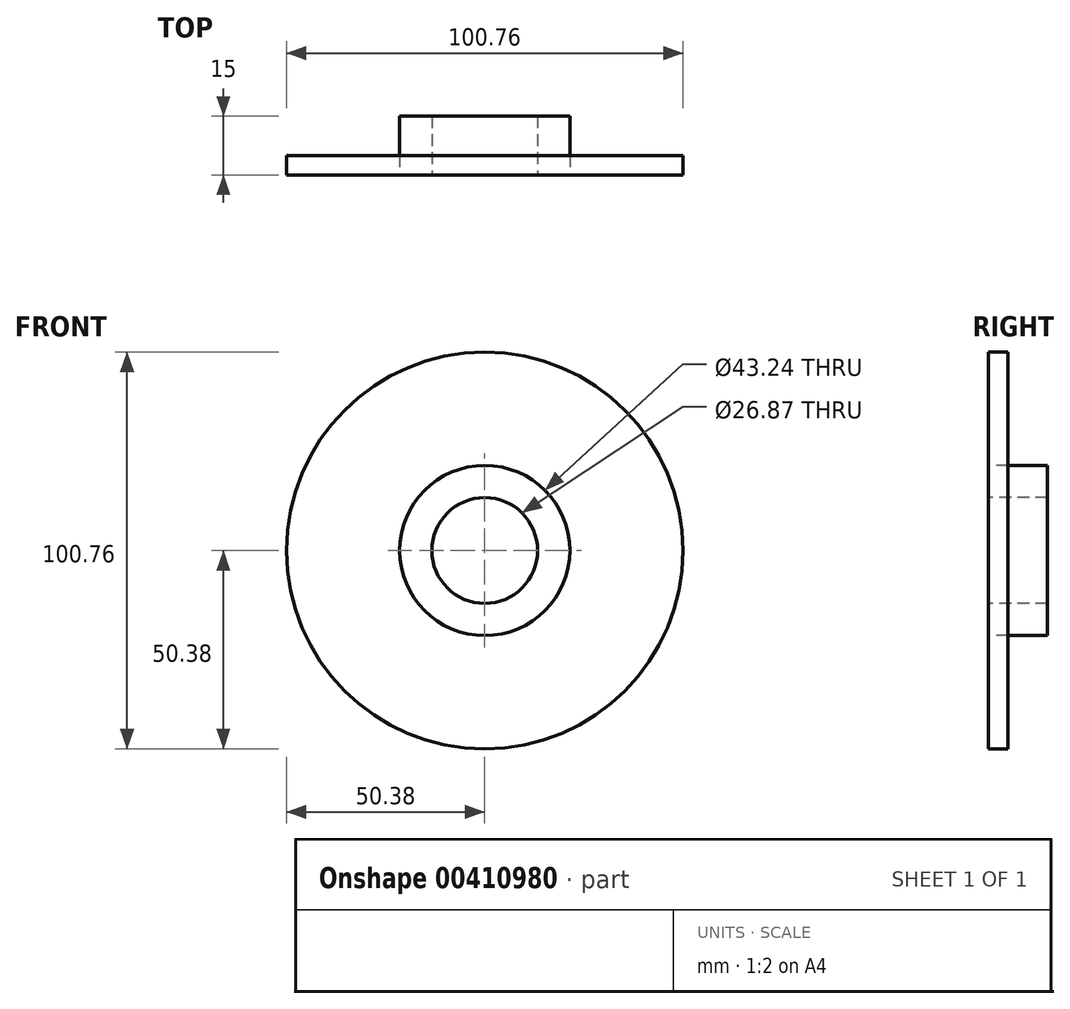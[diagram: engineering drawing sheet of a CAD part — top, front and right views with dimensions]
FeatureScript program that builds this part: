
annotation { "Feature Type Name" : "Feature", "Feature Type Description" : "" }
export const myFeature = defineFeature(function(context is Context, id is Id, definition is map)
    precondition{}
    {
        {
            var Q0;
            Q0=qCreatedBy(makeId("Front.planeOp"),FACE);
            var sketch = newSketch(context, id + "F0", { "sketchPlane" : qUnion([Q0])});
            skCircle(sketch, "E0", {"center": v(0, 0) * mm, "radius": 50.38 * mm});
            skCircle(sketch, "E1", {"center": v(0, 0) * mm, "radius": 13.44 * mm});
            skCircle(sketch, "E2", {"center": v(0, 0) * mm, "radius": 21.62 * mm});
            skLineSegment(sketch, "E3", {"start": v(0, 50.38) * mm, "end": v(-1.45, 50.36) * mm});
            skLineSegment(sketch, "E4.MirrorCS", {"start": v(0, 50.38) * mm, "end": v(1.45, 50.35) * mm});
            skLineSegment(sketch, "E5.MirrorCS", {"start": v(1.45, 50.35) * mm, "end": v(0.15, 48.73) * mm});
            skLineSegment(sketch, "E6.MirrorCS", {"start": v(-1.45, 50.35) * mm, "end": v(-0.15, 48.73) * mm});
            skLineSegment(sketch, "E7", {"start": v(-0.15, 48.73) * mm, "end": v(0.15, 48.73) * mm});
            skSolve(sketch);
        }
        {
            var Q0;
            Q0=makeQuery(id+"F0.imprint","IMPRINT",FACE,{"disambiguationData":[TD([[makeQuery(id+"F0.imprint","IMPRINT",EDGE,{"derivedFrom":sQuery(id+"F0.wireOp",EDGE,"E1")}),-1.0]])]});
            extrude(context, id + "F1", {"entities" : qUnion([Q0]), "oppositeDirection" : true, "depth" : 15 * mm});
        }
        {
            var Q0;
            Q0 = qSketchRegion(id + "F0", true);
            extrude(context, id + "F2", {"entities" : qUnion([Q0]), "oppositeDirection" : true, "depth" : 5 * mm});
        }
        {
            var Q0;
            Q0=sQuery(id+"F0.wireOp",EDGE,"E5.MirrorCS");
            var Q1;
            Q1=sQuery(id+"F0.wireOp",EDGE,"E7");
            var Q2;
            Q2=sQuery(id+"F0.wireOp",EDGE,"E6.MirrorCS");
            var Q3;
            Q3=sQuery(id+"F0.wireOp",EDGE,"E3");
            var Q4;
            Q4=sQuery(id+"F0.wireOp",EDGE,"E4.MirrorCS");
            extrude(context, id + "F3", {"bodyType" : ToolBodyType.SURFACE, "operationType" : NewBodyOperationType.REMOVE, "surfaceEntities" : qUnion([Q0, Q1, Q2, Q3, Q4]), "oppositeDirection" : true, "depth" : 5 * mm});
        }
    });
